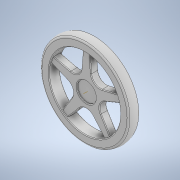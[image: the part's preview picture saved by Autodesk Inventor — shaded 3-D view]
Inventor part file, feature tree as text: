
AUTODESK INVENTOR PART (.ipt)
format: ipt  version: 2022 (Build 260153070, 153G)  size: 443,392 bytes
history: native  units: mm
features: extrude x6, sketch x3, fillet x2, revolve x1, mirror x1
ambient origin geometry x8: Origin, YZ Plane, XZ Plane, XY Plane, X Axis, Y Axis, Z Axis, Center Point
bodies: Solid1 (feature_tree)
feature tree (13):
  extrude  "Extrusion1"  Depth=66.0mm
  sketch  "Sketch2"  dims[d2=8.0mm d3=0.0mm d4=51.8mm]
  extrude  "Extrusion6"  Depth=8.0mm
  extrude  "Extrusion2"  Depth=1.5mm
  extrude  "Extrusion3"  Depth=1.5mm
  extrude  "Extrusion4"  Depth=1.5mm
  extrude  "Extrusion5"  Depth=1.5mm
  fillet  "Fillet1"  Radius=3.7mm
  revolve  "Revolution1"  Angle=360.0deg
  mirror  "Mirror1"
  fillet  "Fillet2"  Radius=6.5mm
  sketch  "Sketch1"  dims[d0=51.8mm d1=66.0mm]
  sketch  "Sketch3"  dims[d5=13.8mm d6=12.566371mm d7=5.0mm d8=3.5mm d9=5.4mm d10=3.7mm d11=50.0mm d13=360.0deg d15=6.5mm d16=0.0mm d17=8.0mm d18=0.0mm d19=1.25mm d20=0.0mm d21=2.225mm d22=0.0mm d23=0.5mm d24=1.25mm d25=90.0deg d26=1.5mm d27=4.725mm d28=0.0mm]
